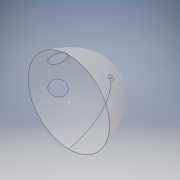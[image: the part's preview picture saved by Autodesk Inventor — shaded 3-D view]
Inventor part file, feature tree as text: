
AUTODESK INVENTOR PART (.ipt)
format: ipt  version: 2018 (Build 220112000, 112)  size: 323,584 bytes
history: native  units: mm
features: sketch x4, extrude x2, revolve x1, shell x1
ambient origin geometry x8: Origin, YZ Plane, XZ Plane, XY Plane, X Axis, Y Axis, Z Axis, Center Point
bodies: Solid1 (feature_tree)
feature tree (8):
  revolve  "Revolution1"  [1 undecoded]
  shell  "Shell1"  Thickness=50.0mm
  extrude  "Extrusion1"  Depth=5.0mm
  sketch  "Sketch3"  dims[d9=30.0mm d10=10.0mm d11=0.0mm]
  extrude  "Extrusion2"  Depth=10.0mm TaperAngle=0.0deg
  sketch  "Sketch1"  dims[d0=750.0mm d1=400.0mm d2=150.0mm d3=350.0mm d4=0.0mm d5=50.0mm d6=50.0mm]
  sketch  "Sketch2"  dims[d7=90.0deg d8=5.0mm]
  sketch  "Sketch4"  dims[d12=250.0mm d13=10.0mm d14=0.0mm]
note: 1 required parameter value undecoded (feature->parameter linkage not recoverable at this tier; creation-order binding heuristic only, values carry confidence <= 0.55)
